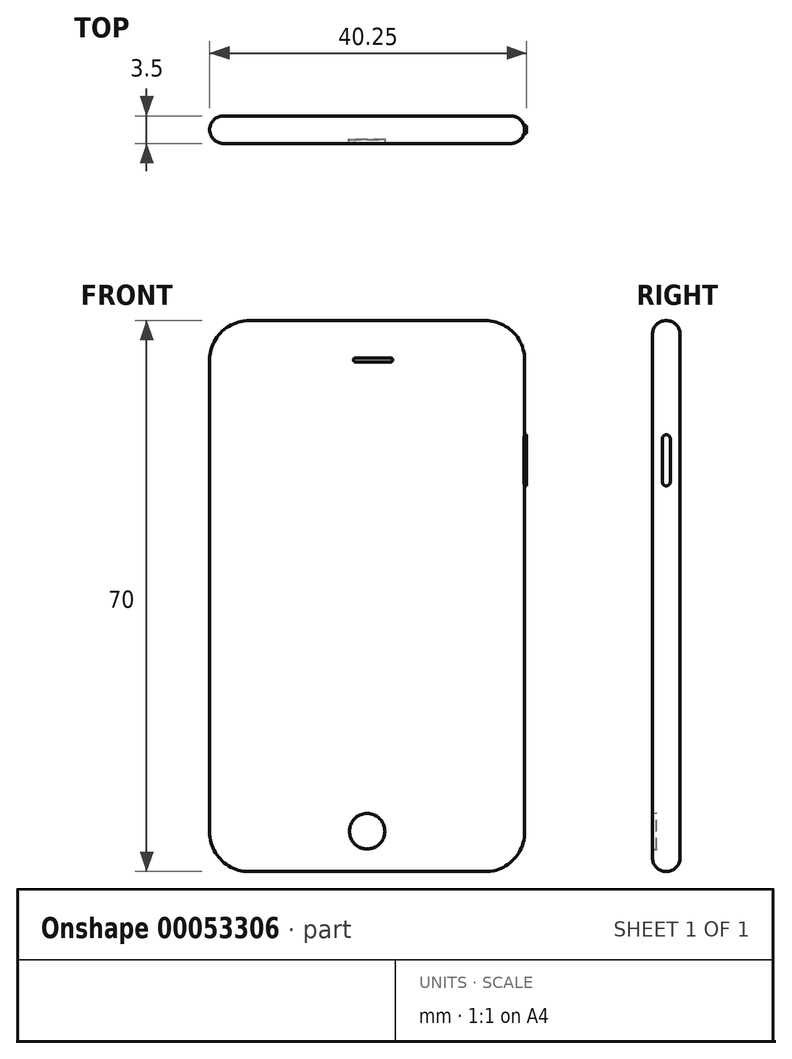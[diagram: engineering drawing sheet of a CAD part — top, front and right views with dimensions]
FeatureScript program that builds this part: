
annotation { "Feature Type Name" : "Feature", "Feature Type Description" : "" }
export const myFeature = defineFeature(function(context is Context, id is Id, definition is map)
    precondition{}
    {
        {
            var Q0;
            Q0=qCreatedBy(makeId("Front.planeOp"),FACE);
            var sketch = newSketch(context, id + "F0", { "sketchPlane" : qUnion([Q0])});
            skLineSegment(sketch, "E0.bottom", {"start": v(5, 0) * mm, "end": v(35, 0) * mm});
            skLineSegment(sketch, "E0.top", {"start": v(5, 70) * mm, "end": v(35, 70) * mm});
            skLineSegment(sketch, "E0.left", {"start": v(0, 5) * mm, "end": v(0, 65) * mm});
            skLineSegment(sketch, "E0.right", {"start": v(40, 5) * mm, "end": v(40, 65) * mm});
            skPoint(sketch, "E1.visualSharp", {"position": v(0, 70) * mm});
            skArc(sketch, "E1.filletArc", {"start": v(5, 70) * mm, "mid": v(1.46, 68.54) * mm, "end": v(0, 65) * mm});
            skPoint(sketch, "E2.visualSharp", {"position": v(40, 70) * mm});
            skArc(sketch, "E2.filletArc", {"start": v(40, 65) * mm, "mid": v(38.54, 68.54) * mm, "end": v(35, 70) * mm});
            skPoint(sketch, "E3.visualSharp", {"position": v(40, 0) * mm});
            skArc(sketch, "E3.filletArc", {"start": v(35, 0) * mm, "mid": v(38.54, 1.46) * mm, "end": v(40, 5) * mm});
            skPoint(sketch, "E4.visualSharp", {"position": v(0, 0) * mm});
            skArc(sketch, "E4.filletArc", {"start": v(0, 5) * mm, "mid": v(1.46, 1.46) * mm, "end": v(5, 0) * mm});
            skSolve(sketch);
        }
        {
            var Q0;
            Q0=makeQuery(id+"F0.imprint","IMPRINT",FACE,{"disambiguationData":[TD([[makeQuery(id+"F0.imprint","IMPRINT",EDGE,{"derivedFrom":sQuery(id+"F0.wireOp",EDGE,"E0.bottom")}),1.0]])]});
            extrude(context, id + "F1", {"entities" : qUnion([Q0]), "depth" : 3.5 * mm});
        }
        {
            var Q0;
            Q0=makeQuery(id+"F1.opExtrude","CAP_FACE",FACE,{"disambiguationData":[OSD([sQuery(id+"F0.wireOp",EDGE,"E0.bottom"),sQuery(id+"F0.wireOp",EDGE,"E0.top"),sQuery(id+"F0.wireOp",EDGE,"E0.left"),sQuery(id+"F0.wireOp",EDGE,"E0.right"),sQuery(id+"F0.wireOp",EDGE,"E1.filletArc"),sQuery(id+"F0.wireOp",EDGE,"E2.filletArc"),sQuery(id+"F0.wireOp",EDGE,"E3.filletArc"),sQuery(id+"F0.wireOp",EDGE,"E4.filletArc")])],"isStart":false});
            fillet(context, id + "F2", {"entities" : qUnion([Q0]), "radius" : 1.75 * mm, "tangentPropagation" : true, "allowEdgeOverflow" : false});
        }
        {
            var Q0;
            Q0=makeQuery(id+"F1.opExtrude","CAP_FACE",FACE,{"disambiguationData":[OSD([sQuery(id+"F0.wireOp",EDGE,"E0.bottom"),sQuery(id+"F0.wireOp",EDGE,"E0.top"),sQuery(id+"F0.wireOp",EDGE,"E0.left"),sQuery(id+"F0.wireOp",EDGE,"E0.right"),sQuery(id+"F0.wireOp",EDGE,"E1.filletArc"),sQuery(id+"F0.wireOp",EDGE,"E2.filletArc"),sQuery(id+"F0.wireOp",EDGE,"E3.filletArc"),sQuery(id+"F0.wireOp",EDGE,"E4.filletArc")])],"isStart":true});
            var Q1;
            Q1=makeQuery(id+"F1.opExtrude","CAP_FACE",FACE,{"disambiguationData":[OSD([sQuery(id+"F0.wireOp",EDGE,"E0.bottom"),sQuery(id+"F0.wireOp",EDGE,"E0.top"),sQuery(id+"F0.wireOp",EDGE,"E0.left"),sQuery(id+"F0.wireOp",EDGE,"E0.right"),sQuery(id+"F0.wireOp",EDGE,"E1.filletArc"),sQuery(id+"F0.wireOp",EDGE,"E2.filletArc"),sQuery(id+"F0.wireOp",EDGE,"E3.filletArc"),sQuery(id+"F0.wireOp",EDGE,"E4.filletArc")])],"isStart":false});
            fillet(context, id + "F3", {"entities" : qUnion([Q0, Q1]), "radius" : 1.75 * mm, "tangentPropagation" : true, "allowEdgeOverflow" : false});
        }
        {
            var Q0;
            Q0=makeQuery(id+"F1.opExtrude","CAP_FACE",FACE,{"disambiguationData":[OSD([sQuery(id+"F0.wireOp",EDGE,"E0.bottom"),sQuery(id+"F0.wireOp",EDGE,"E0.top"),sQuery(id+"F0.wireOp",EDGE,"E0.left"),sQuery(id+"F0.wireOp",EDGE,"E0.right"),sQuery(id+"F0.wireOp",EDGE,"E1.filletArc"),sQuery(id+"F0.wireOp",EDGE,"E2.filletArc"),sQuery(id+"F0.wireOp",EDGE,"E3.filletArc"),sQuery(id+"F0.wireOp",EDGE,"E4.filletArc")])],"isStart":false});
            var sketch = newSketch(context, id + "F4", { "sketchPlane" : qUnion([Q0])});
            skCircle(sketch, "E5", {"center": v(20, 5.12) * mm, "radius": 2.25 * mm});
            skSolve(sketch);
        }
        {
            var Q0;
            Q0=makeQuery(id+"F4.imprint","IMPRINT",FACE,{"disambiguationData":[TD([[makeQuery(id+"F4.imprint","IMPRINT",EDGE,{"derivedFrom":sQuery(id+"F4.wireOp",EDGE,"E5")}),1.0]])]});
            extrude(context, id + "F5", {"entities" : qUnion([Q0]), "operationType" : NewBodyOperationType.REMOVE, "oppositeDirection" : true, "depth" : .5 * mm, "hasDraft" : true, "draftAngle" : 10 * degree});
        }
        {
            var Q0;
            Q0=makeQuery(id+"F1.opExtrude","CAP_FACE",FACE,{"disambiguationData":[OSD([sQuery(id+"F0.wireOp",EDGE,"E0.bottom"),sQuery(id+"F0.wireOp",EDGE,"E0.top"),sQuery(id+"F0.wireOp",EDGE,"E0.left"),sQuery(id+"F0.wireOp",EDGE,"E0.right"),sQuery(id+"F0.wireOp",EDGE,"E1.filletArc"),sQuery(id+"F0.wireOp",EDGE,"E2.filletArc"),sQuery(id+"F0.wireOp",EDGE,"E3.filletArc"),sQuery(id+"F0.wireOp",EDGE,"E4.filletArc")])],"isStart":false});
            var sketch = newSketch(context, id + "F6", { "sketchPlane" : qUnion([Q0])});
            skLineSegment(sketch, "E6.bottom", {"start": v(18.5, 64.75) * mm, "end": v(23, 64.75) * mm});
            skLineSegment(sketch, "E6.top", {"start": v(18.5, 65.25) * mm, "end": v(23, 65.25) * mm});
            skArc(sketch, "E7", {"start": v(23, 64.75) * mm, "mid": v(23.25, 65) * mm, "end": v(23, 65.25) * mm});
            skArc(sketch, "E8", {"start": v(18.5, 64.75) * mm, "mid": v(18.25, 65) * mm, "end": v(18.5, 65.25) * mm});
            skSolve(sketch);
        }
        {
            var Q0;
            Q0 = qSketchRegion(id + "F6", true);
            extrude(context, id + "F7", {"entities" : qUnion([Q0]), "operationType" : NewBodyOperationType.REMOVE, "oppositeDirection" : true, "depth" : .1 * mm});
        }
        {
            var Q0;
            Q0=makeQuery(id+"F6.imprint","IMPRINT",FACE,{"disambiguationData":[TD([[makeQuery(id+"F6.imprint","IMPRINT",EDGE,{"derivedFrom":sQuery(id+"F6.wireOp",EDGE,"E6.bottom")}),-1.0]])]});
            var sketch = newSketch(context, id + "F8", { "sketchPlane" : qUnion([Q0])});
            skLineSegment(sketch, "E9.bottom", {"start": v(4.5, 10.25) * mm, "end": v(37, 10.25) * mm});
            skLineSegment(sketch, "E9.top", {"start": v(4.5, 60.25) * mm, "end": v(37, 60.25) * mm});
            skLineSegment(sketch, "E9.left", {"start": v(4.5, 10.25) * mm, "end": v(4.5, 60.25) * mm});
            skLineSegment(sketch, "E9.right", {"start": v(37, 10.25) * mm, "end": v(37, 60.25) * mm});
            skSolve(sketch);
        }
        {
            var Q0;
            Q0=qCreatedBy(makeId("Right.planeOp"),FACE);
            cPlane(context, id + "F9", {"entities" : qUnion([Q0]), "cplaneType" : CPlaneType.OFFSET, "offset" : 39 * mm, "width" : 150 * mm, "height" : 150 * mm});
        }
        {
            var Q0;
            Q0=qCreatedBy(id+"F9.planeOp",FACE);
            var sketch = newSketch(context, id + "F10", { "sketchPlane" : qUnion([Q0])});
            skLineSegment(sketch, "E10", {"start": v(-2.25, 55) * mm, "end": v(-2.25, 49.5) * mm});
            skLineSegment(sketch, "E11", {"start": v(-1.25, 55) * mm, "end": v(-1.25, 49.5) * mm});
            skArc(sketch, "E12", {"start": v(-2.25, 55) * mm, "mid": v(-1.75, 55.5) * mm, "end": v(-1.25, 55) * mm});
            skArc(sketch, "E13", {"start": v(-2.25, 49.5) * mm, "mid": v(-1.75, 49) * mm, "end": v(-1.25, 49.5) * mm});
            skSolve(sketch);
        }
        {
            var Q0;
            Q0 = qSketchRegion(id + "F10", true);
            extrude(context, id + "F11", {"entities" : qUnion([Q0]), "operationType" : NewBodyOperationType.ADD, "depth" : 1.25 * mm});
        }
    });
